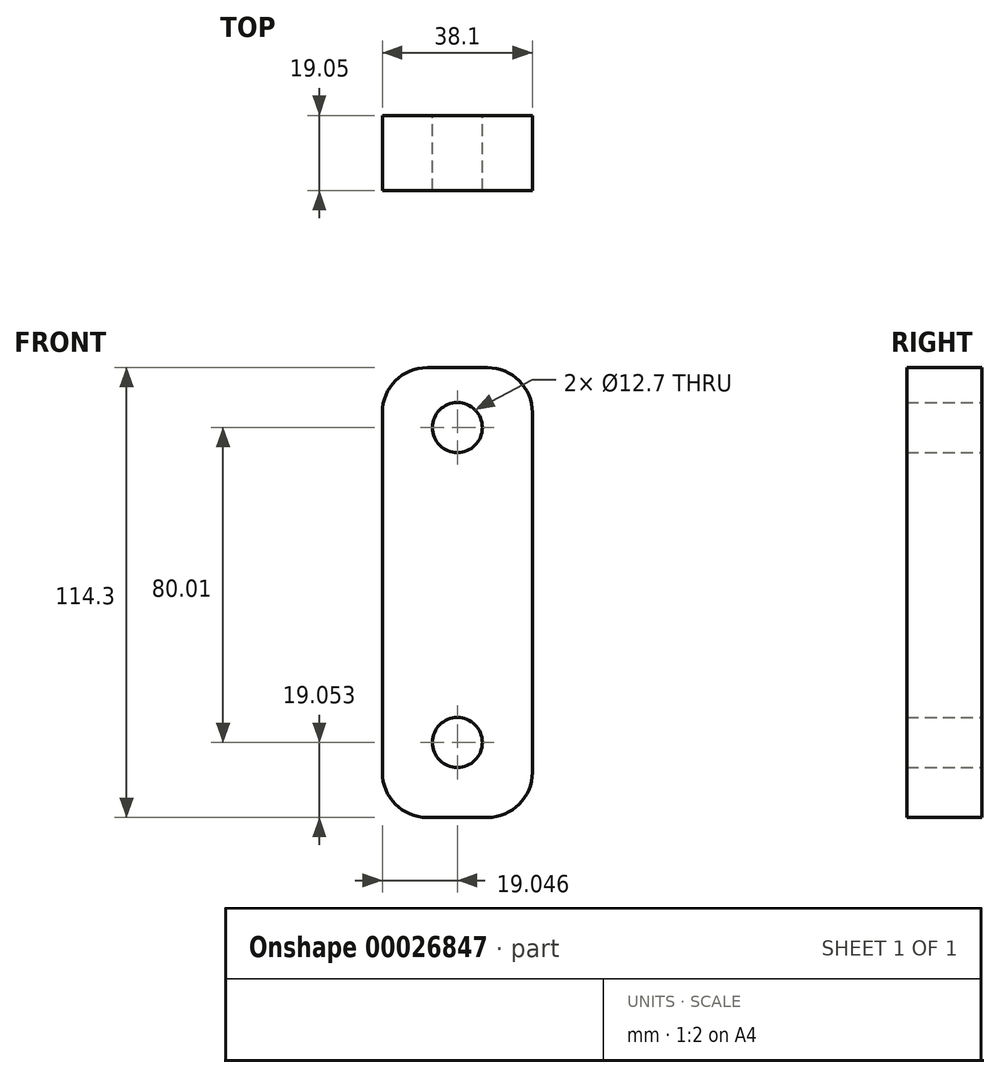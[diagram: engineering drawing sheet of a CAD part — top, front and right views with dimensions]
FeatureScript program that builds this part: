
annotation { "Feature Type Name" : "Feature", "Feature Type Description" : "" }
export const myFeature = defineFeature(function(context is Context, id is Id, definition is map)
    precondition{}
    {
        {
            var Q0;
            Q0=qCreatedBy(makeId("Front.planeOp"),FACE);
            var sketch = newSketch(context, id + "F0", { "sketchPlane" : qUnion([Q0])});
            skLineSegment(sketch, "E0.bottom", {"start": v(1.9, 52.9) * mm, "end": v(17.15, 52.9) * mm});
            skLineSegment(sketch, "E0.top", {"start": v(1.9, -61.4) * mm, "end": v(17.15, -61.4) * mm});
            skLineSegment(sketch, "E0.left", {"start": v(-9.52, 41.47) * mm, "end": v(-9.52, -49.97) * mm});
            skLineSegment(sketch, "E0.right", {"start": v(28.58, 41.47) * mm, "end": v(28.58, -49.97) * mm});
            skCircle(sketch, "E1", {"center": v(9.53, -42.35) * mm, "radius": 6.35 * mm});
            skPoint(sketch, "E2.visualSharp", {"position": v(-9.52, 52.9) * mm});
            skArc(sketch, "E2.filletArc", {"start": v(1.9, 52.9) * mm, "mid": v(-6.18, 49.56) * mm, "end": v(-9.52, 41.47) * mm});
            skPoint(sketch, "E3.visualSharp", {"position": v(28.58, 52.9) * mm});
            skArc(sketch, "E3.filletArc", {"start": v(28.58, 41.47) * mm, "mid": v(25.23, 49.56) * mm, "end": v(17.15, 52.9) * mm});
            skPoint(sketch, "E4.visualSharp", {"position": v(-9.52, -61.4) * mm});
            skArc(sketch, "E4.filletArc", {"start": v(-9.52, -49.97) * mm, "mid": v(-6.18, -58.05) * mm, "end": v(1.9, -61.4) * mm});
            skPoint(sketch, "E5.visualSharp", {"position": v(28.58, -61.4) * mm});
            skArc(sketch, "E5.filletArc", {"start": v(17.15, -61.4) * mm, "mid": v(25.23, -58.05) * mm, "end": v(28.58, -49.97) * mm});
            skCircle(sketch, "E6", {"center": v(9.53, 37.66) * mm, "radius": 6.35 * mm});
            skSolve(sketch);
        }
        {
            var Q0;
            Q0 = qSketchRegion(id + "F0", true);
            extrude(context, id + "F1", {"entities" : qUnion([Q0]), "depth" : 19.05 * mm});
        }
    });
